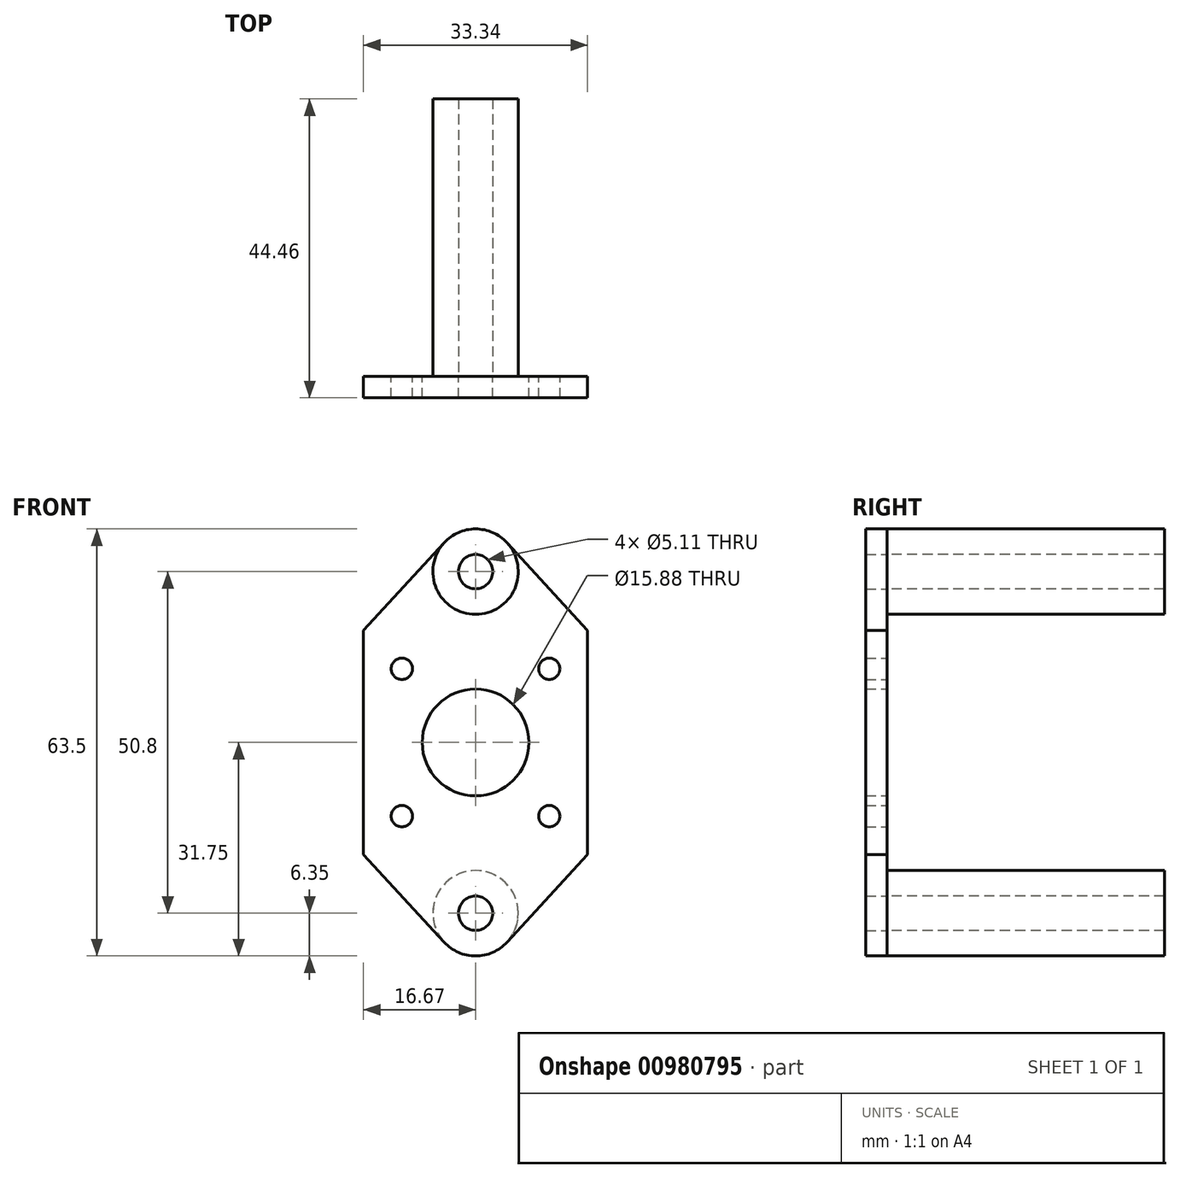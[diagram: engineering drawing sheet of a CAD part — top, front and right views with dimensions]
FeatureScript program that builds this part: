
annotation { "Feature Type Name" : "Feature", "Feature Type Description" : "" }
export const myFeature = defineFeature(function(context is Context, id is Id, definition is map)
    precondition{}
    {
        {
            var Q0;
            Q0=qCreatedBy(makeId("Front.planeOp"),FACE);
            var sketch = newSketch(context, id + "F0", { "sketchPlane" : qUnion([Q0])});
            skCircle(sketch, "E0", {"center": v(0, 25.4) * mm, "radius": 2.55 * mm});
            skCircle(sketch, "E1", {"center": v(0, -25.4) * mm, "radius": 2.55 * mm});
            skLineSegment(sketch, "E2", {"start": v(0, -25.4) * mm, "end": v(0, 0) * mm, "construction": true});
            skLineSegment(sketch, "E3", {"start": v(0, 25.4) * mm, "end": v(0, 0) * mm, "construction": true});
            skCircle(sketch, "E4", {"center": v(0, -25.4) * mm, "radius": 6.35 * mm, "construction": true});
            skCircle(sketch, "E5", {"center": v(0, 25.4) * mm, "radius": 6.35 * mm, "construction": true});
            skArc(sketch, "E6", {"start": v(-4.67, 29.7) * mm, "mid": v(0, 31.75) * mm, "end": v(4.67, 29.7) * mm});
            skLineSegment(sketch, "E7", {"start": v(4.67, 29.7) * mm, "end": v(16.67, 16.67) * mm});
            skLineSegment(sketch, "E8", {"start": v(16.67, 16.67) * mm, "end": v(16.67, -16.67) * mm});
            skLineSegment(sketch, "E9", {"start": v(16.67, -16.67) * mm, "end": v(4.67, -29.7) * mm});
            skArc(sketch, "E10", {"start": v(4.67, -29.7) * mm, "mid": v(0, -31.75) * mm, "end": v(-4.67, -29.7) * mm});
            skLineSegment(sketch, "E11", {"start": v(-4.67, -29.7) * mm, "end": v(-16.67, -16.67) * mm});
            skLineSegment(sketch, "E12", {"start": v(-16.67, -16.67) * mm, "end": v(-16.67, 16.67) * mm});
            skLineSegment(sketch, "E13", {"start": v(-16.67, 16.67) * mm, "end": v(-4.67, 29.7) * mm});
            skLineSegment(sketch, "E14", {"start": v(-16.67, 0) * mm, "end": v(0, 0) * mm, "construction": true});
            skLineSegment(sketch, "E15", {"start": v(0, 0) * mm, "end": v(16.67, 0) * mm, "construction": true});
            skLineSegment(sketch, "E16.bottom", {"start": v(-16.67, 16.67) * mm, "end": v(16.67, 16.67) * mm, "construction": true});
            skLineSegment(sketch, "E16.top", {"start": v(-16.67, -16.67) * mm, "end": v(16.67, -16.67) * mm, "construction": true});
            skLineSegment(sketch, "E16.left", {"start": v(-16.67, 16.67) * mm, "end": v(-16.67, -16.67) * mm, "construction": true});
            skLineSegment(sketch, "E16.right", {"start": v(16.67, 16.67) * mm, "end": v(16.67, -16.67) * mm, "construction": true});
            skPoint(sketch, "E16.middle", {"position": v(0, 0) * mm});
            skLineSegment(sketch, "E17.bottom", {"start": v(-10.96, 10.96) * mm, "end": v(10.96, 10.96) * mm, "construction": true});
            skLineSegment(sketch, "E17.top", {"start": v(-10.96, -10.96) * mm, "end": v(10.96, -10.96) * mm, "construction": true});
            skLineSegment(sketch, "E17.left", {"start": v(-10.96, 10.96) * mm, "end": v(-10.96, -10.96) * mm, "construction": true});
            skLineSegment(sketch, "E17.right", {"start": v(10.96, 10.96) * mm, "end": v(10.96, -10.96) * mm, "construction": true});
            skCircle(sketch, "E18", {"center": v(-10.96, 10.96) * mm, "radius": 1.59 * mm});
            skCircle(sketch, "E19", {"center": v(-10.96, -10.96) * mm, "radius": 1.59 * mm});
            skCircle(sketch, "E20", {"center": v(10.96, -10.96) * mm, "radius": 1.59 * mm});
            skCircle(sketch, "E21", {"center": v(10.96, 10.96) * mm, "radius": 1.59 * mm});
            skCircle(sketch, "E22", {"center": v(0, 0) * mm, "radius": 7.94 * mm});
            skSolve(sketch);
        }
        {
            var Q0;
            Q0 = qSketchRegion(id + "F0", true);
            extrude(context, id + "F1", {"entities" : qUnion([Q0]), "depth" : 3.17 * mm, "offsetDistance" : 25.4 * mm});
        }
        {
            var Q0;
            Q0=makeQuery(id+"F1.opExtrude","CAP_FACE",FACE,{"disambiguationData":[OSD([sQuery(id+"F0.wireOp",EDGE,"E0"),sQuery(id+"F0.wireOp",EDGE,"E1"),sQuery(id+"F0.wireOp",EDGE,"E6"),sQuery(id+"F0.wireOp",EDGE,"E7"),sQuery(id+"F0.wireOp",EDGE,"E8"),sQuery(id+"F0.wireOp",EDGE,"E9"),sQuery(id+"F0.wireOp",EDGE,"E10"),sQuery(id+"F0.wireOp",EDGE,"E11"),sQuery(id+"F0.wireOp",EDGE,"E12"),sQuery(id+"F0.wireOp",EDGE,"E13"),sQuery(id+"F0.wireOp",EDGE,"E18"),sQuery(id+"F0.wireOp",EDGE,"E19"),sQuery(id+"F0.wireOp",EDGE,"E20"),sQuery(id+"F0.wireOp",EDGE,"E21"),sQuery(id+"F0.wireOp",EDGE,"E22")])],"isStart":true});
            var sketch = newSketch(context, id + "F2", { "sketchPlane" : qUnion([Q0])});
            skCircle(sketch, "E23", {"center": v(0, 25.4) * mm, "radius": 6.35 * mm});
            skCircle(sketch, "E24", {"center": v(0, -25.4) * mm, "radius": 6.35 * mm});
            skCircle(sketch, "E25", {"center": v(0, 25.4) * mm, "radius": 2.55 * mm});
            skCircle(sketch, "E26", {"center": v(0, -25.4) * mm, "radius": 2.55 * mm});
            skSolve(sketch);
        }
        {
            var Q0;
            Q0 = qSketchRegion(id + "F2", true);
            extrude(context, id + "F3", {"entities" : qUnion([Q0]), "depth" : 41.27 * mm, "offsetDistance" : 25.4 * mm});
        }
    });
